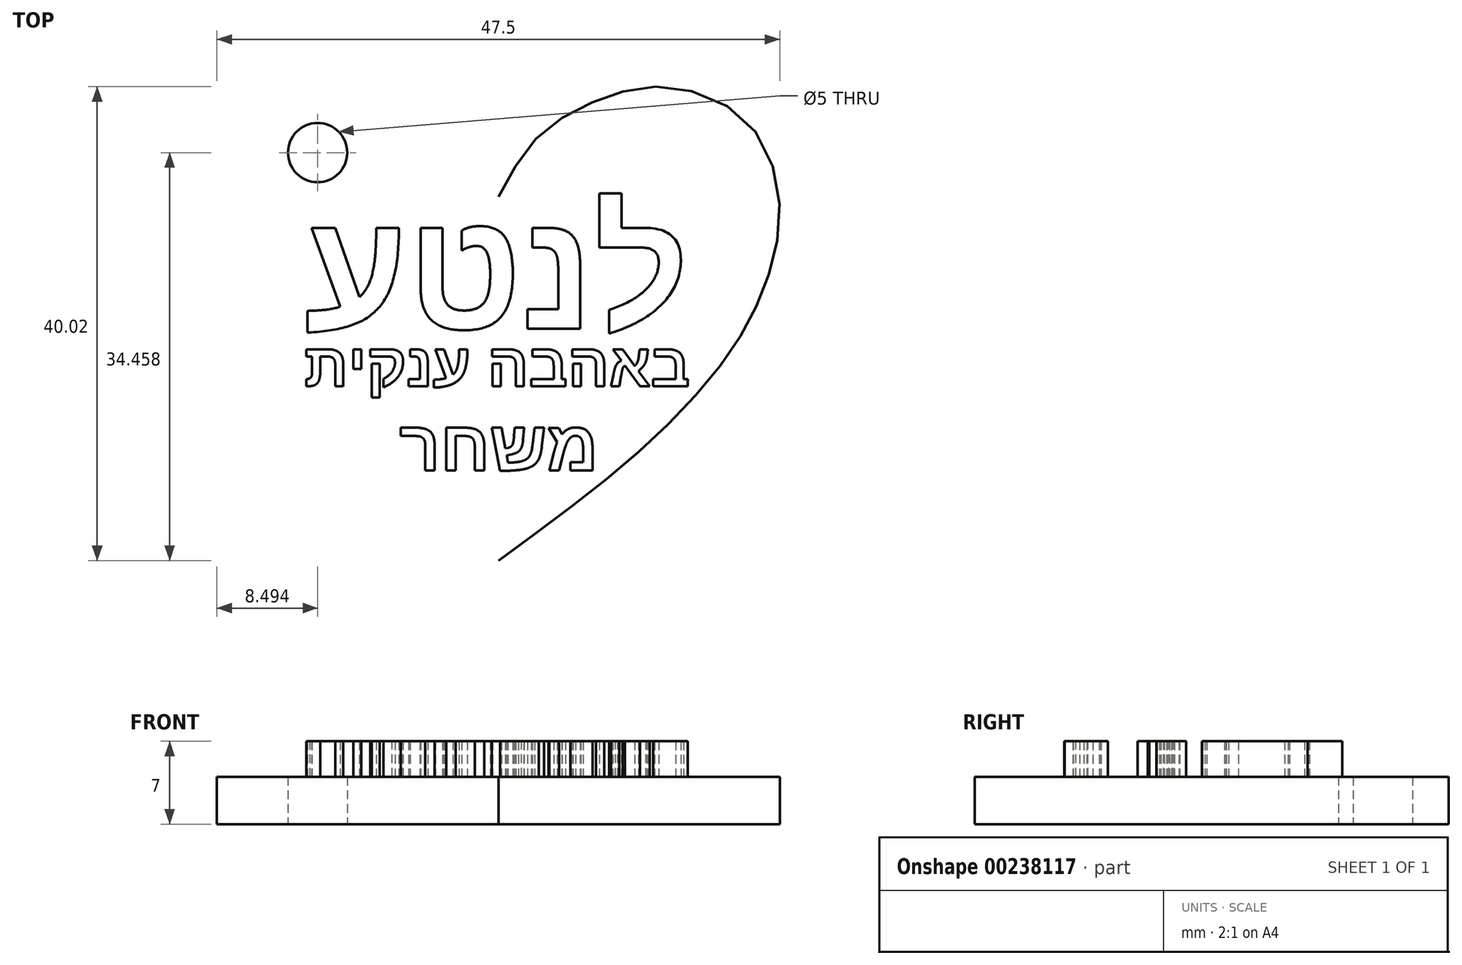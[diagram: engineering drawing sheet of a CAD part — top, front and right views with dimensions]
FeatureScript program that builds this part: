
annotation { "Feature Type Name" : "Feature", "Feature Type Description" : "" }
export const myFeature = defineFeature(function(context is Context, id is Id, definition is map)
    precondition{}
    {
        {
            var Q0;
            Q0=qCreatedBy(makeId("Top.planeOp"),FACE);
            var sketch = newSketch(context, id + "F0", { "sketchPlane" : qUnion([Q0])});
            skPoint(sketch, "E0.10.internal.snap0", {"position": v(0, -25.36) * mm});
            skFitSpline(sketch, "E0", {"points": [v(0, 5.37) * mm, v(-3.45, 10.54) * mm, v(-8.48, 13.58) * mm, v(-14.05, 14.64) * mm, v(-20.82, 11.87) * mm, v(-23.72, 4.97) * mm, v(-22.66, -1.66) * mm, v(-20.01, -7.1) * mm, v(-15.24, -12.92) * mm, v(-8.61, -18.89) * mm, v(0, -25.36) * mm], "startDerivative": vector(-32.37, 60.4) * mm, "endDerivative": vector(72.39, -52.67) * mm});
            skLineSegment(sketch, "E1", {"start": v(0, 5.37) * mm, "end": v(0, -25.36) * mm, "construction": true});
            skFitSpline(sketch, "E2.MirrorCS", {"points": [v(0, 5.37) * mm, v(3.45, 10.54) * mm, v(8.48, 13.58) * mm, v(14.05, 14.64) * mm, v(20.82, 11.87) * mm, v(23.72, 4.97) * mm, v(22.66, -1.66) * mm, v(20.01, -7.1) * mm, v(15.24, -12.92) * mm, v(8.61, -18.89) * mm, v(0, -25.36) * mm], "startDerivative": vector(32.37, 60.4) * mm, "endDerivative": vector(-72.39, -52.67) * mm});
            skCircle(sketch, "E3", {"center": v(-15.26, 9.1) * mm, "radius": 2.5 * mm});
            skSolve(sketch);
        }
        {
            var Q0;
            Q0 = qSketchRegion(id + "F0", true);
            extrude(context, id + "F1", {"entities" : qUnion([Q0]), "depth" : 4 * mm});
        }
        {
            var Q0;
            Q0=makeQuery(id+"F1.opExtrude","CAP_FACE",FACE,{"disambiguationData":[OSD([sQuery(id+"F0.wireOp",EDGE,"E0"),sQuery(id+"F0.wireOp",EDGE,"E2.MirrorCS"),sQuery(id+"F0.wireOp",EDGE,"E3")])],"isStart":false});
            var sketch = newSketch(context, id + "F2", { "sketchPlane" : qUnion([Q0])});
            skText(sketch, "E4", { "text": "עטנל", "fontName": "Arimo-Bold.ttf"});
            skText(sketch, "E5", { "text": "תיקנע הבהאב", "fontName": "Arimo-Bold.ttf"});
            skText(sketch, "E6", { "text": "רחשמ", "fontName": "Arimo-Bold.ttf"});
            const initialGuessF2  = {"E4": [-0.01638, -0.00577, 1, 0, 0.01012], "E5": [-0.01638, -0.01063, 1, 0, 0.00371], "E6": [-0.00834, -0.01775, 1, 0, 0.0043]};
            skSetInitialGuess(sketch, initialGuessF2);
            skSolve(sketch);
        }
        {
            var Q0;
            Q0 = qSketchRegion(id + "F2", true);
            extrude(context, id + "F3", {"entities" : qUnion([Q0]), "operationType" : NewBodyOperationType.ADD, "depth" : 3 * mm});
        }
    });
